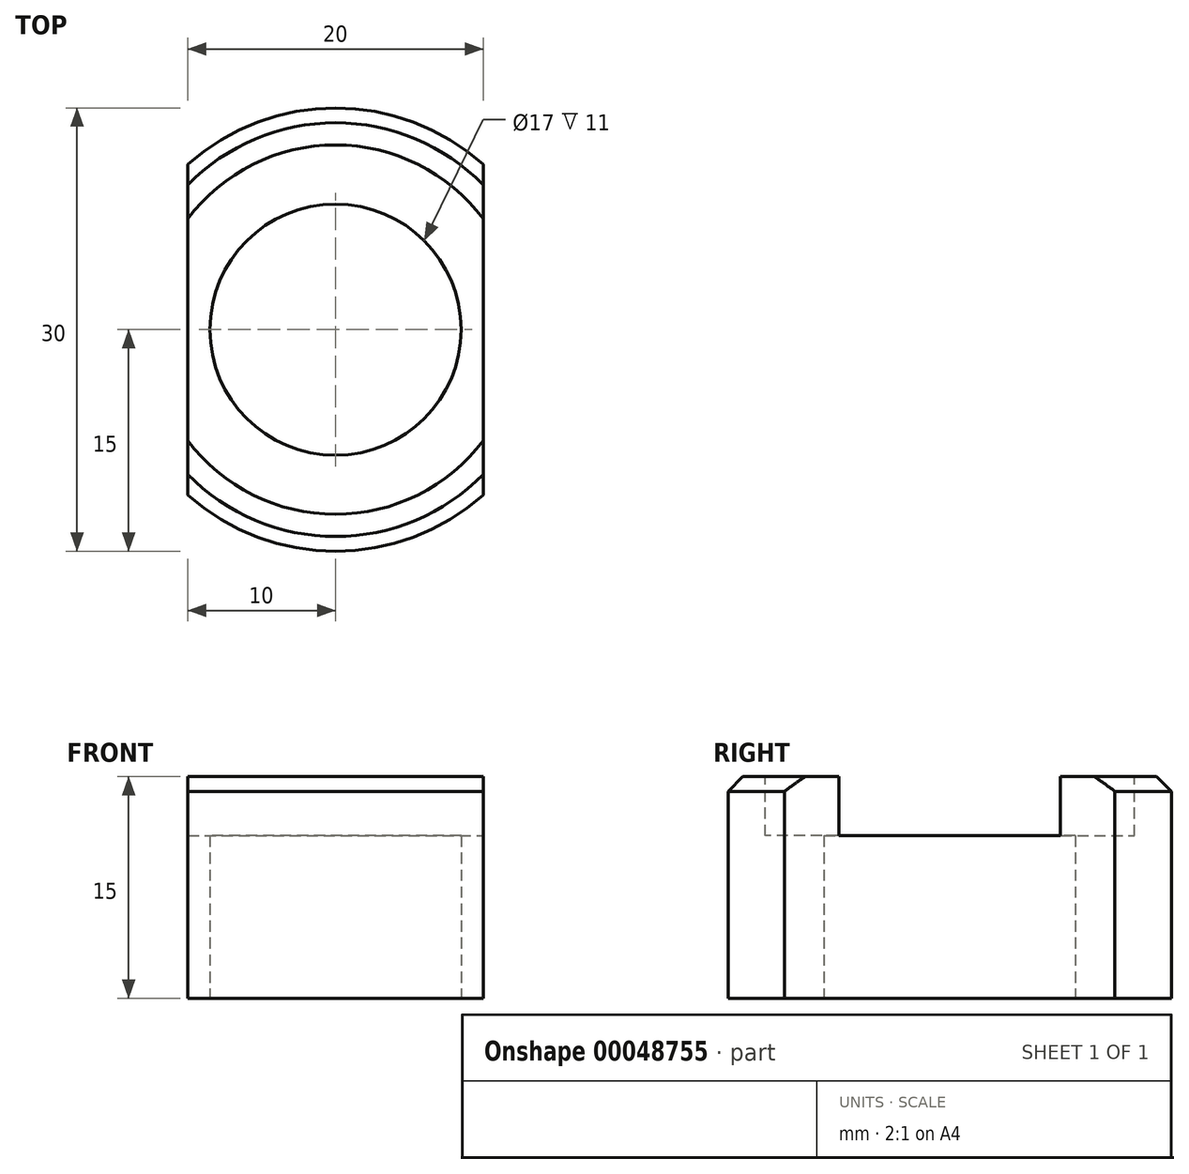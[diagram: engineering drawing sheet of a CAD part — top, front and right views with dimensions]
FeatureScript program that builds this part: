
annotation { "Feature Type Name" : "Feature", "Feature Type Description" : "" }
export const myFeature = defineFeature(function(context is Context, id is Id, definition is map)
    precondition{}
    {
        {
            var Q0;
            Q0=qCreatedBy(makeId("Top.planeOp"),FACE);
            var sketch = newSketch(context, id + "F0", { "sketchPlane" : qUnion([Q0])});
            skCircle(sketch, "E0", {"center": v(0, 0) * mm, "radius": 8.5 * mm});
            skCircle(sketch, "E1", {"center": v(0, 0) * mm, "radius": 15 * mm});
            skPoint(sketch, "E2", {"position": v(-10, 0) * mm});
            skLineSegment(sketch, "E3", {"start": v(-10, 11.18) * mm, "end": v(-10, -11.18) * mm});
            skLineSegment(sketch, "E4.MirrorCS", {"start": v(10, 11.18) * mm, "end": v(10, -11.18) * mm});
            skSolve(sketch);
        }
        {
            var Q0;
            Q0=makeQuery(id+"F0.imprint","IMPRINT",FACE,{"disambiguationData":[TD([[makeQuery(id+"F0.imprint","IMPRINT",EDGE,{"derivedFrom":sQuery(id+"F0.wireOp",EDGE,"E0")}),-1.0]])]});
            extrude(context, id + "F1", {"entities" : qUnion([Q0]), "offsetDistance" : 25 * mm, "depth" : 15 * mm});
        }
        {
            var Q0;
            Q0=makeQuery(id+"F1.opExtrude","CAP_FACE",FACE,{"disambiguationData":[OSD([sQuery(id+"F0.wireOp",EDGE,"E0"),sQuery(id+"F0.wireOp",EDGE,"E1")])],"isStart":false});
            var sketch = newSketch(context, id + "F2", { "sketchPlane" : qUnion([Q0])});
            skCircle(sketch, "E5", {"center": v(0, 0) * mm, "radius": 12.5 * mm});
            skSolve(sketch);
        }
        {
            var Q0;
            Q0=makeQuery(id+"F2.imprint","IMPRINT",FACE,{"disambiguationData":[TD([[makeQuery(id+"F2.imprint","IMPRINT",EDGE,{"derivedFrom":sQuery(id+"F2.wireOp",EDGE,"E5")}),1.0]])]});
            extrude(context, id + "F3", {"entities" : qUnion([Q0]), "operationType" : NewBodyOperationType.REMOVE, "oppositeDirection" : true, "offsetDistance" : 25 * mm, "depth" : 4 * mm});
        }
        {
            var Q0;
            Q0=makeQuery(id+"F1.opExtrude","CAP_EDGE",EDGE,{"disambiguationData":[OSD([sQuery(id+"F0.wireOp",EDGE,"E1")])],"isStart":false});
            chamfer(context, id + "F4", {"entities" : qUnion([Q0]), "width" : 1 * mm, "tangentPropagation" : true});
        }
    });
